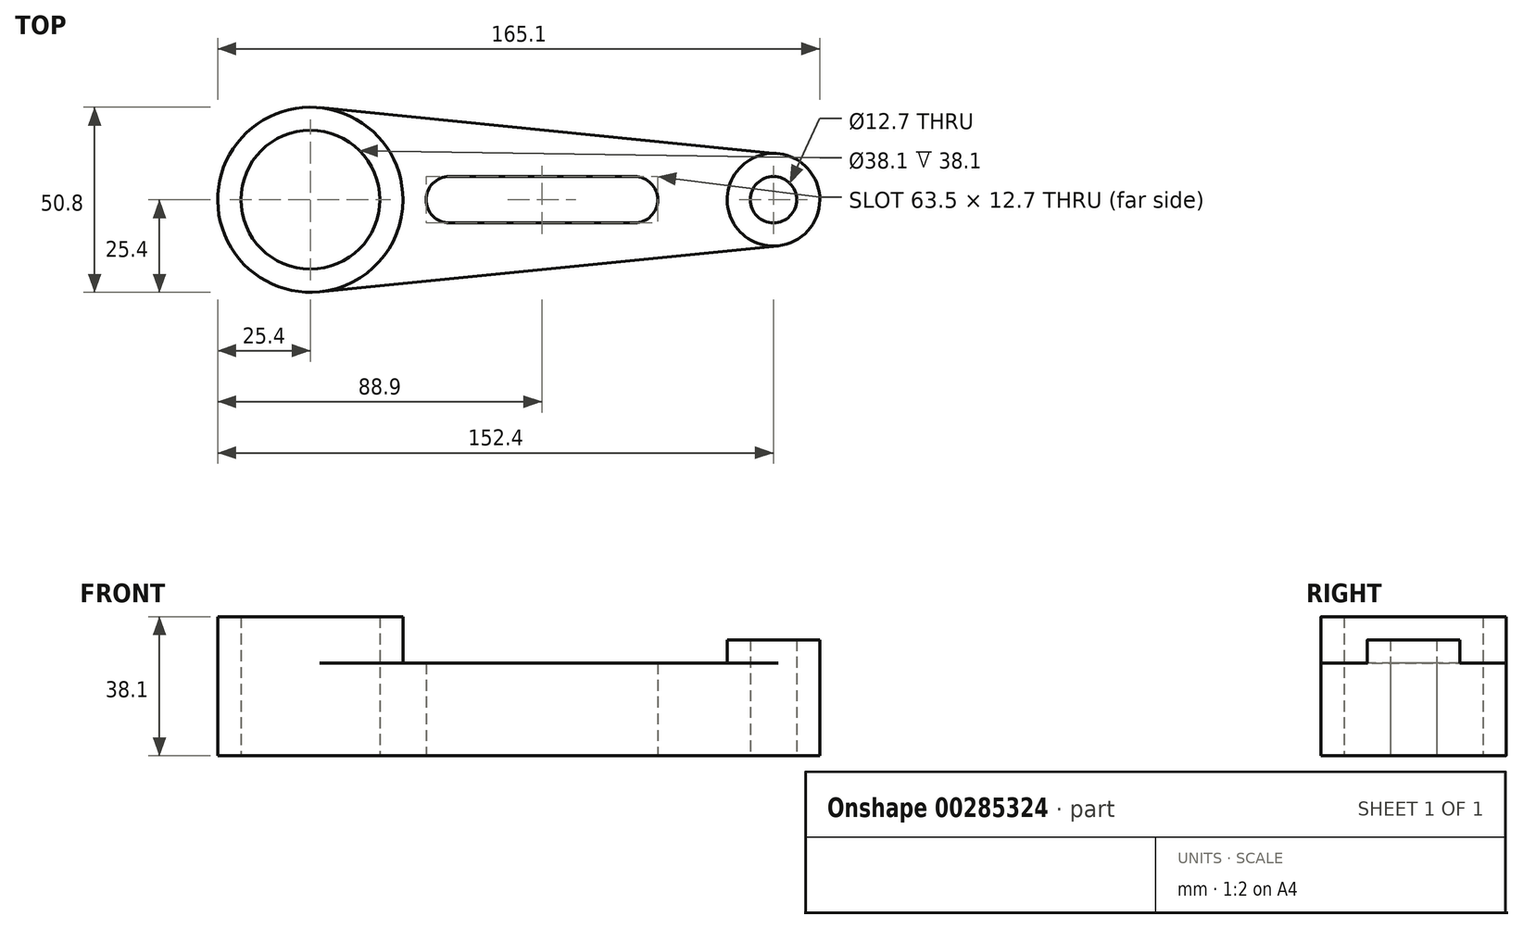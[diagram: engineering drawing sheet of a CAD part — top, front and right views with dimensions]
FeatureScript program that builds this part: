
annotation { "Feature Type Name" : "Feature", "Feature Type Description" : "" }
export const myFeature = defineFeature(function(context is Context, id is Id, definition is map)
    precondition{}
    {
        {
            var Q0;
            Q0=qCreatedBy(makeId("Top.planeOp"),FACE);
            var sketch = newSketch(context, id + "F0", { "sketchPlane" : qUnion([Q0])});
            skCircle(sketch, "E0", {"center": v(-103.86, 0) * mm, "radius": 25.4 * mm});
            skCircle(sketch, "E1", {"center": v(-103.86, 0) * mm, "radius": 19.05 * mm});
            skCircle(sketch, "E2", {"center": v(23.14, 0) * mm, "radius": 12.7 * mm});
            skCircle(sketch, "E3", {"center": v(23.14, 0) * mm, "radius": 6.35 * mm});
            skLineSegment(sketch, "E4", {"start": v(-101.32, 25.27) * mm, "end": v(24.4, 12.64) * mm});
            skLineSegment(sketch, "E5", {"start": v(-101.32, -25.27) * mm, "end": v(24.4, -12.64) * mm});
            skLineSegment(sketch, "E6", {"start": v(-65.76, 6.35) * mm, "end": v(-65.76, 6.35) * mm});
            skLineSegment(sketch, "E7", {"start": v(-65.76, -6.35) * mm, "end": v(-14.96, -6.35) * mm});
            skLineSegment(sketch, "E8", {"start": v(-103.86, 0) * mm, "end": v(23.14, 0) * mm, "construction": true});
            skLineSegment(sketch, "E9", {"start": v(-65.76, 6.35) * mm, "end": v(-14.96, 6.35) * mm});
            skArc(sketch, "E10", {"start": v(-65.76, -6.35) * mm, "mid": v(-59.41, 0) * mm, "end": v(-65.76, 6.35) * mm, "construction": true});
            skArc(sketch, "E11", {"start": v(-65.76, 6.35) * mm, "mid": v(-72.11, 0) * mm, "end": v(-65.76, -6.35) * mm});
            skArc(sketch, "E12", {"start": v(-14.96, 6.35) * mm, "mid": v(-21.31, 0) * mm, "end": v(-14.96, -6.35) * mm, "construction": true});
            skArc(sketch, "E13", {"start": v(-14.96, -6.35) * mm, "mid": v(-8.61, 0) * mm, "end": v(-14.96, 6.35) * mm});
            skSolve(sketch);
        }
        {
            var Q0;
            {var subQ3=sQuery(id+"F0.wireOp",EDGE,"E4");Q0=makeQuery(id+"F0.imprint","IMPRINT",FACE,{"disambiguationData":[TD([[makeQuery(id+"F0.imprint","IMPRINT",EDGE,{"derivedFrom":subQ3}),-1.0]])]});}
            var Q1;
            Q1=makeQuery(id+"F0.imprint","IMPRINT",FACE,{"disambiguationData":[TD([[makeQuery(id+"F0.imprint","IMPRINT",EDGE,{"derivedFrom":sQuery(id+"F0.wireOp",EDGE,"E1")}),-1.0]])]});
            var Q2;
            Q2=makeQuery(id+"F0.imprint","IMPRINT",FACE,{"disambiguationData":[TD([[makeQuery(id+"F0.imprint","IMPRINT",EDGE,{"derivedFrom":sQuery(id+"F0.wireOp",EDGE,"E3")}),-1.0]])]});
            extrude(context, id + "F1", {"entities" : qUnion([Q0, Q1, Q2]), "depth" : 25.4 * mm});
        }
        {
            var Q0;
            Q0=makeQuery(id+"F1.opExtrude","CAP_FACE",FACE,{"disambiguationData":[OSD([sQuery(id+"F0.wireOp",EDGE,"E0"),sQuery(id+"F0.wireOp",EDGE,"E1"),sQuery(id+"F0.wireOp",EDGE,"E2"),sQuery(id+"F0.wireOp",EDGE,"E3"),sQuery(id+"F0.wireOp",EDGE,"E4"),sQuery(id+"F0.wireOp",EDGE,"E5"),sQuery(id+"F0.wireOp",EDGE,"E7"),sQuery(id+"F0.wireOp",EDGE,"E9"),sQuery(id+"F0.wireOp",EDGE,"E11"),sQuery(id+"F0.wireOp",EDGE,"E13")])],"isStart":false});
            var sketch = newSketch(context, id + "F2", { "sketchPlane" : qUnion([Q0])});
            skCircle(sketch, "E14", {"center": v(-103.86, 0) * mm, "radius": 25.4 * mm});
            skSolve(sketch);
        }
        {
            var Q0;
            Q0=makeQuery(id+"F2.imprint","IMPRINT",FACE,{"disambiguationData":[TD([[makeQuery(id+"F2.imprint","IMPRINT",EDGE,{"derivedFrom":makeQuery(id+"F1.opExtrude","CAP_EDGE",EDGE,{"disambiguationData":[OSD([sQuery(id+"F0.wireOp",EDGE,"E1")])],"isStart":false})}),-1.0]])]});
            extrude(context, id + "F3", {"entities" : qUnion([Q0]), "operationType" : NewBodyOperationType.ADD, "depth" : 12.7 * mm});
        }
        {
            var Q0;
            Q0=makeQuery(id+"F1.opExtrude","CAP_FACE",FACE,{"disambiguationData":[OSD([sQuery(id+"F0.wireOp",EDGE,"E0"),sQuery(id+"F0.wireOp",EDGE,"E1"),sQuery(id+"F0.wireOp",EDGE,"E2"),sQuery(id+"F0.wireOp",EDGE,"E3"),sQuery(id+"F0.wireOp",EDGE,"E4"),sQuery(id+"F0.wireOp",EDGE,"E5"),sQuery(id+"F0.wireOp",EDGE,"E7"),sQuery(id+"F0.wireOp",EDGE,"E9"),sQuery(id+"F0.wireOp",EDGE,"E11"),sQuery(id+"F0.wireOp",EDGE,"E13")])],"isStart":false});
            var sketch = newSketch(context, id + "F4", { "sketchPlane" : qUnion([Q0])});
            skCircle(sketch, "E15", {"center": v(23.14, 0) * mm, "radius": 12.7 * mm});
            skSolve(sketch);
        }
        {
            var Q0;
            Q0=makeQuery(id+"F4.imprint","IMPRINT",FACE,{"disambiguationData":[TD([[makeQuery(id+"F4.imprint","IMPRINT",EDGE,{"derivedFrom":makeQuery(id+"F1.opExtrude","CAP_EDGE",EDGE,{"disambiguationData":[OSD([sQuery(id+"F0.wireOp",EDGE,"E3")])],"isStart":false})}),-1.0]])]});
            extrude(context, id + "F5", {"entities" : qUnion([Q0]), "operationType" : NewBodyOperationType.ADD, "depth" : 6.35 * mm});
        }
    });
